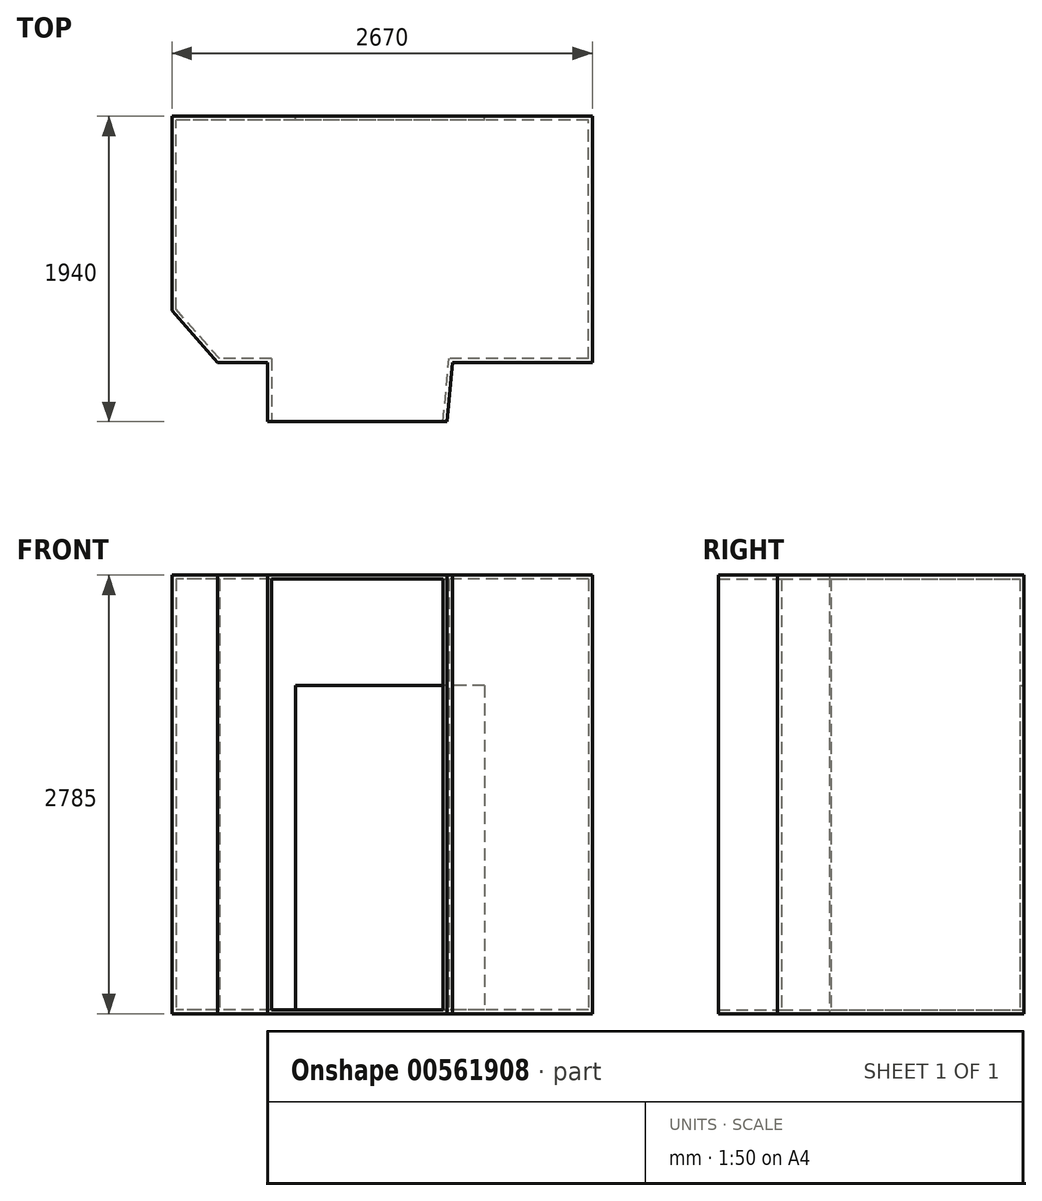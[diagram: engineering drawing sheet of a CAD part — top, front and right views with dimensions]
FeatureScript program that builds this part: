
annotation { "Feature Type Name" : "Feature", "Feature Type Description" : "" }
export const myFeature = defineFeature(function(context is Context, id is Id, definition is map)
    precondition{}
    {
        {
            var Q0;
            Q0=qCreatedBy(makeId("Top.planeOp"),FACE);
            var sketch = newSketch(context, id + "F0", { "sketchPlane" : qUnion([Q0])});
            skLineSegment(sketch, "E0.bottom", {"start": v(0, 0) * mm, "end": v(-885, 0) * mm});
            skLineSegment(sketch, "E0.top", {"start": v(0, 1515) * mm, "end": v(-2620, 1515) * mm});
            skLineSegment(sketch, "E0.left", {"start": v(0, 0) * mm, "end": v(0, 1515) * mm});
            skLineSegment(sketch, "E0.right", {"start": v(-2620, 315) * mm, "end": v(-2620, 1515) * mm});
            skLineSegment(sketch, "E1", {"start": v(-2342.2, 0) * mm, "end": v(-2620, 315) * mm});
            skLineSegment(sketch, "E2", {"start": v(-2012.2, 0) * mm, "end": v(-2012.2, -400) * mm});
            skLineSegment(sketch, "E3", {"start": v(-2012.2, -400) * mm, "end": v(-922.2, -400) * mm});
            skLineSegment(sketch, "E4", {"start": v(-922.2, -400) * mm, "end": v(-885, 0) * mm});
            skLineSegment(sketch, "E5.trimOffspring", {"start": v(-2012.2, 0) * mm, "end": v(-2342.2, 0) * mm});
            skSolve(sketch);
        }
        {
            var Q0;
            Q0=makeQuery(id+"F0.imprint","IMPRINT",FACE,{"disambiguationData":[TD([[makeQuery(id+"F0.imprint","IMPRINT",EDGE,{"derivedFrom":sQuery(id+"F0.wireOp",EDGE,"E0.bottom")}),-1.0]])]});
            extrude(context, id + "F1", {"entities" : qUnion([Q0]), "depth" : 2735 * mm, "offsetDistance" : 25 * mm});
        }
        {
            var Q0;
            Q0=makeQuery(id+"F1.opExtrude","SWEPT_FACE",FACE,{"disambiguationData":[OSD([sQuery(id+"F0.wireOp",EDGE,"E3")])]});
            shell(context, id + "F2", {"entities" : qUnion([Q0]), "thickness" : 25 * mm, "oppositeDirection" : true});
        }
        {
            var Q0;
            Q0=makeQuery(id+"F1.opExtrude","SWEPT_FACE",FACE,{"disambiguationData":[OSD([sQuery(id+"F0.wireOp",EDGE,"E0.top")])]});
            var sketch = newSketch(context, id + "F3", { "sketchPlane" : qUnion([Q0])});
            skLineSegment(sketch, "E6.bottom", {"start": v(660, 2060) * mm, "end": v(1860, 2060) * mm});
            skLineSegment(sketch, "E6.top", {"start": v(660, 0) * mm, "end": v(1860, 0) * mm});
            skLineSegment(sketch, "E6.left", {"start": v(660, 2060) * mm, "end": v(660, 0) * mm});
            skLineSegment(sketch, "E6.right", {"start": v(1860, 2060) * mm, "end": v(1860, 0) * mm});
            skSolve(sketch);
        }
        {
            var Q0;
            Q0=makeQuery(id+"F3.imprint","IMPRINT",FACE,{"disambiguationData":[TD([[makeQuery(id+"F3.imprint","IMPRINT",EDGE,{"derivedFrom":sQuery(id+"F3.wireOp",EDGE,"E6.bottom")}),-1.0]])]});
            var Q1;
            Q1=makeQuery(id+"F2.opShell","OFFSET_FACE",FACE,{"disambiguationData":[OSD([sQuery(id+"F0.wireOp",EDGE,"E0.top")])]});
            extrude(context, id + "F4", {"entities" : qUnion([Q0]), "operationType" : NewBodyOperationType.REMOVE, "endBound" : BoundingType.UP_TO_SURFACE, "oppositeDirection" : true, "depth" : 25 * mm, "endBoundEntityFace" : qUnion([Q1]), "offsetDistance" : 25 * mm});
        }
    });
